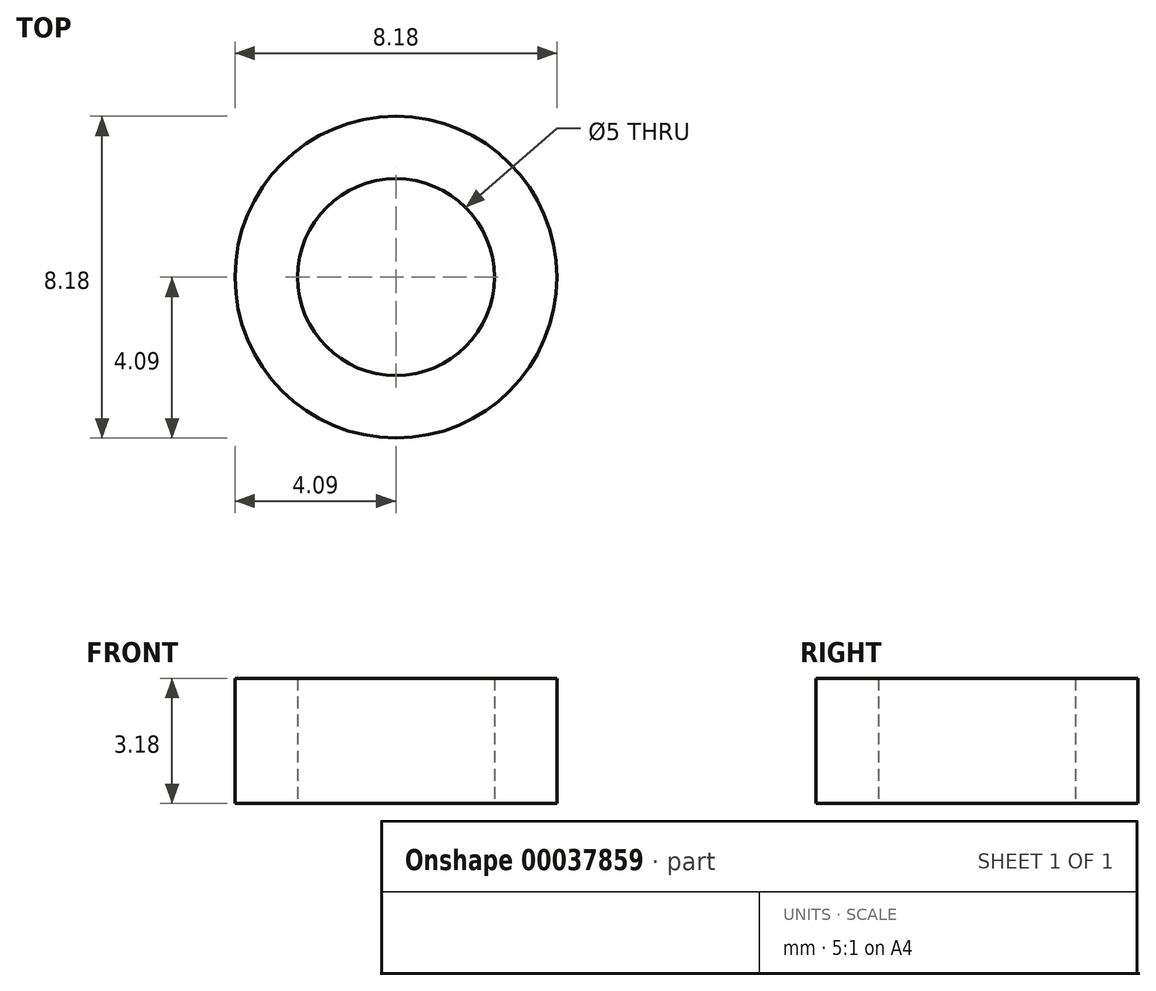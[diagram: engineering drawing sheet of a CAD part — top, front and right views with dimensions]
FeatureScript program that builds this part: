
annotation { "Feature Type Name" : "Feature", "Feature Type Description" : "" }
export const myFeature = defineFeature(function(context is Context, id is Id, definition is map)
    precondition{}
    {
        {
            var Q0;
            Q0=qCreatedBy(makeId("Top.planeOp"),FACE);
            var sketch = newSketch(context, id + "F0", { "sketchPlane" : qUnion([Q0])});
            skCircle(sketch, "E0", {"center": v(0, 0) * mm, "radius": 2.5 * mm});
            skCircle(sketch, "E1", {"center": v(0, 0) * mm, "radius": 4.09 * mm});
            skSolve(sketch);
        }
        {
            var Q0;
            Q0 = qSketchRegion(id + "F0", true);
            extrude(context, id + "F1", {"entities" : qUnion([Q0]), "depth" : 3.17 * mm});
        }
    });
